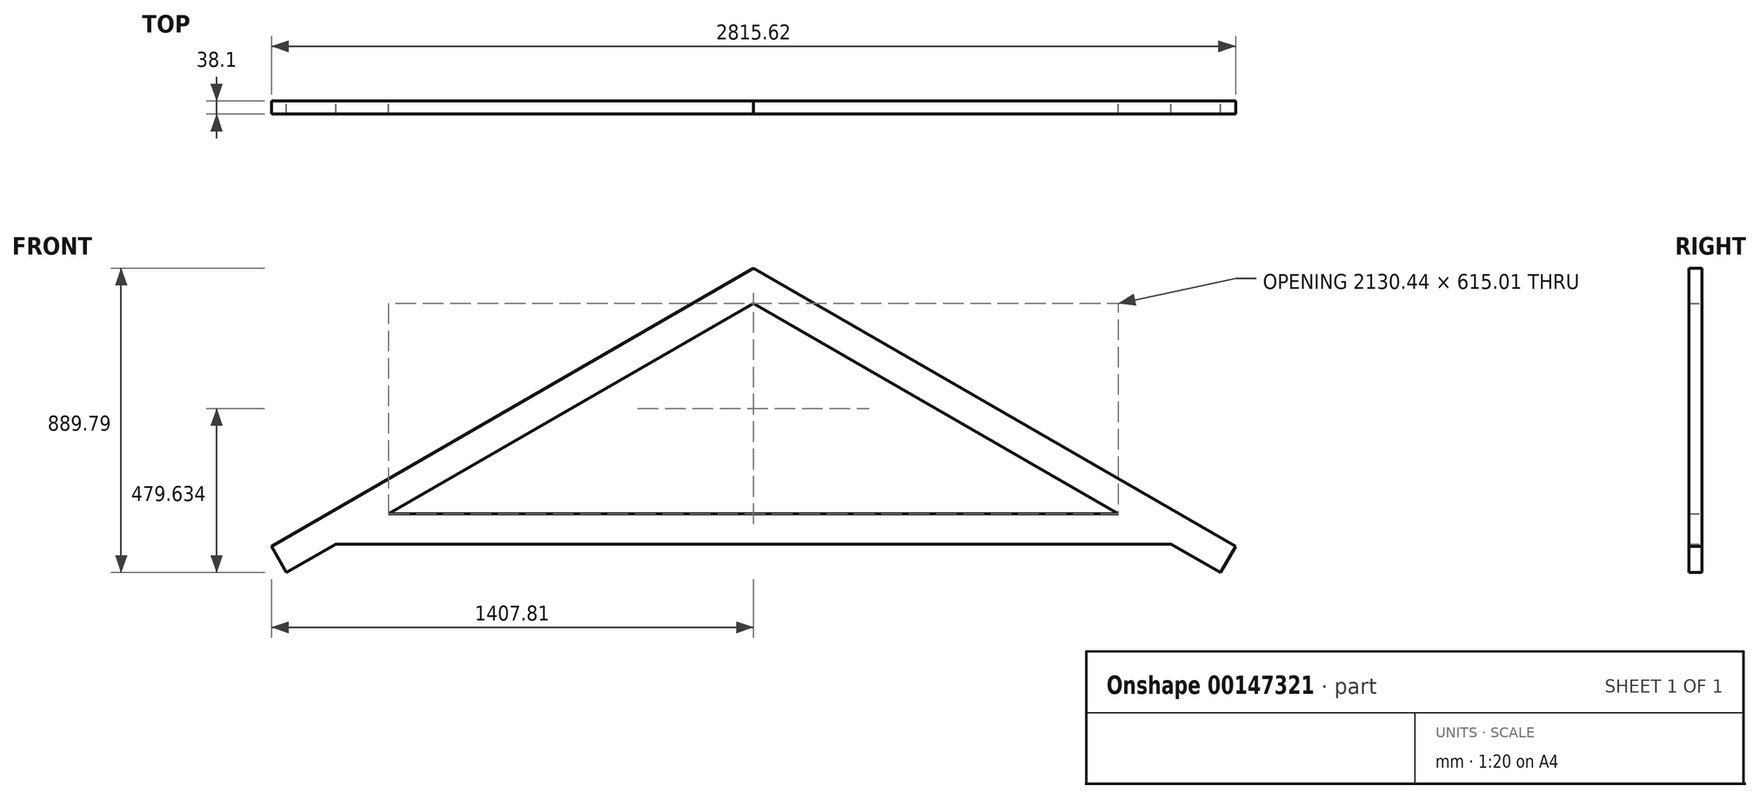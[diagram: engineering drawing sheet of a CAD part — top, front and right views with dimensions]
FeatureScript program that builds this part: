
annotation { "Feature Type Name" : "Feature", "Feature Type Description" : "" }
export const myFeature = defineFeature(function(context is Context, id is Id, definition is map)
    precondition{}
    {
        {
            var Q0;
            Q0=qCreatedBy(makeId("Front.planeOp"),FACE);
            var sketch = newSketch(context, id + "F0", { "sketchPlane" : qUnion([Q0])});
            skLineSegment(sketch, "E0.bottom", {"start": v(-1036.7, -52.67) * mm, "end": v(1093.73, -52.67) * mm});
            skLineSegment(sketch, "E0.top", {"start": v(-1190.69, -141.57) * mm, "end": v(1247.71, -141.57) * mm});
            skLineSegment(sketch, "E1", {"start": v(-1334.85, -224.8) * mm, "end": v(-1190.69, -141.57) * mm});
            skLineSegment(sketch, "E2", {"start": v(1391.87, -224.8) * mm, "end": v(1247.71, -141.57) * mm});
            skLineSegment(sketch, "E3", {"start": v(-1334.85, -224.8) * mm, "end": v(-1379.3, -147.81) * mm});
            skLineSegment(sketch, "E4", {"start": v(-1379.3, -147.81) * mm, "end": v(28.51, 664.99) * mm});
            skLineSegment(sketch, "E5.MirrorCS", {"start": v(1436.32, -147.81) * mm, "end": v(28.51, 664.99) * mm});
            skLineSegment(sketch, "E6.MirrorCS", {"start": v(1391.87, -224.8) * mm, "end": v(1436.32, -147.81) * mm});
            skLineSegment(sketch, "E7.trimOffspring", {"start": v(1093.73, -52.67) * mm, "end": v(28.51, 562.34) * mm});
            skLineSegment(sketch, "E8.trimOffspring", {"start": v(-1036.7, -52.67) * mm, "end": v(28.51, 562.34) * mm});
            skSolve(sketch);
        }
        {
            var Q0;
            Q0=qSketchRegion(id+"F0",true);
            extrude(context, id + "F1", {"entities" : qUnion([Q0]), "endBound" : BoundingType.SYMMETRIC, "depth" : 38.1 * mm});
        }
    });
